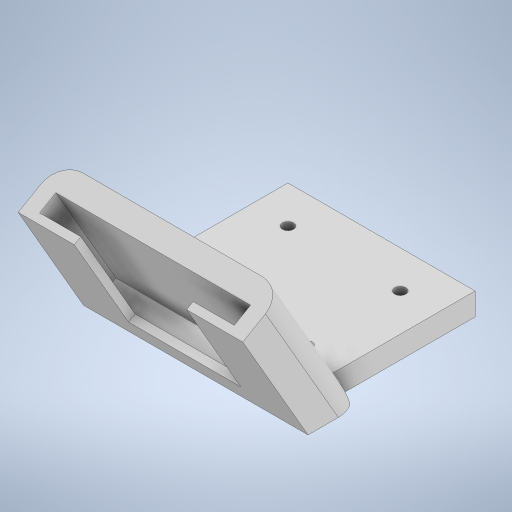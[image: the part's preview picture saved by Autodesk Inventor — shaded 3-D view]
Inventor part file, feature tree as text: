
AUTODESK INVENTOR PART (.ipt)
format: ipt  version: 2024 (Build 280153000, 153)  size: 363,520 bytes
history: native  units: in
note: dims shown in document units (in); Inventor stores cm internally (conversion verified against a paired STEP export)
features: sketch x8, extrude x6, plane x1, sweep x1, fillet x1
ambient origin geometry x8: Origin, YZ Plane, XZ Plane, XY Plane, X Axis, Y Axis, Z Axis, Center Point
bodies: Solid1 (feature_tree)
feature tree (17):
  extrude  "Extrusion1"  Depth=0.5906in
  plane  "Work Plane1"
  extrude  "Extrusion2"  Depth=0.1969in
  extrude  "Extrusion3"  Depth=0.0591in
  extrude  "Extrusion4"  Depth=0.0591in
  extrude  "Extrusion5"  TaperAngle=120.0deg  [1 undecoded]
  sweep  "Sweep1"
  extrude  "Extrusion6"  Depth=0.1181in TaperAngle=0.0deg
  fillet  "Fillet1"  Radius=0.6299in
  sketch  "Sketch1"  dims[d0=0.4921in d1=0.5906in]
  sketch  "Sketch2"  dims[d2=0.1969in d3=0.1969in]
  sketch  "Sketch3"  dims[d4=0.0591in d5=0.0591in]
  sketch  "Sketch4"  dims[d6=0.0591in d7=0.0591in]
  sketch  "Sketch5"  dims[d8=0.1181in d9=0.0in d10=120.0deg]
  sketch  "Sketch6"  dims[d11=0.748in d12=0.6299in]
  sketch  "3D Sketch1"
  sketch  "Sketch7"  dims[d13=1.1811in d14=0.1181in d15=0.0in d16=0.6299in d17=1.0236in d18=0.0787in d19=0.0984in d20=0.0in d21=0.5906in d23=0.1378in d24=0.0394in d25=0.0in d26=0.0394in d27=0.0in d28=0.0in d29=0.0in d30=0.0in d31=0.0in d32=0.1181in]
note: 1 required parameter value undecoded (feature->parameter linkage not recoverable at this tier; creation-order binding heuristic only, values carry confidence <= 0.55)
